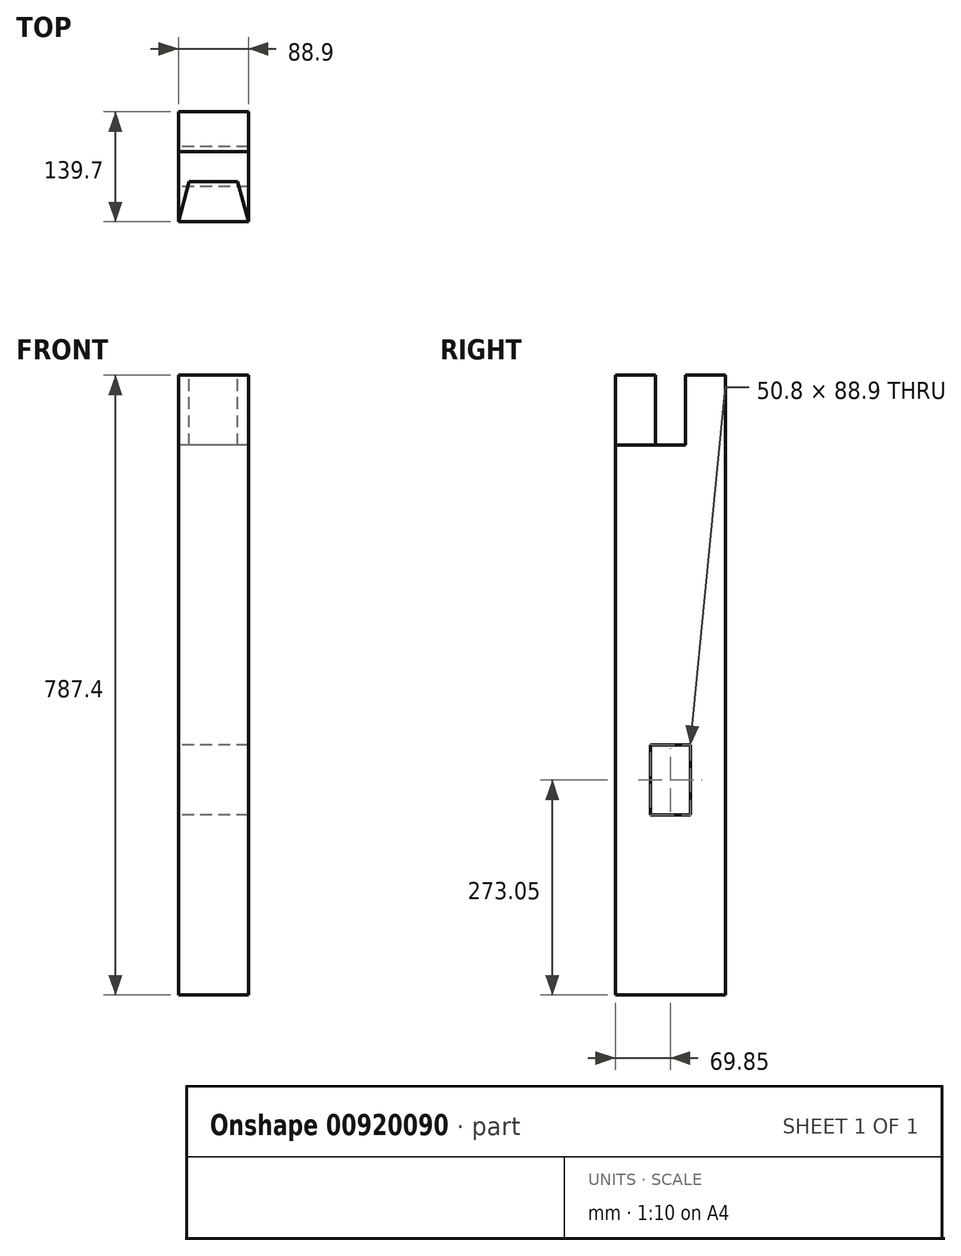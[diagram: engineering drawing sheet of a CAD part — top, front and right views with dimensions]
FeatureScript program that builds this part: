
annotation { "Feature Type Name" : "Feature", "Feature Type Description" : "" }
export const myFeature = defineFeature(function(context is Context, id is Id, definition is map)
    precondition{}
    {
        {
            var Q0;
            Q0=qCreatedBy(makeId("Top.planeOp"),FACE);
            var sketch = newSketch(context, id + "F0", { "sketchPlane" : qUnion([Q0])});
            skLineSegment(sketch, "E0.bottom", {"start": v(0, 0) * mm, "end": v(88.9, 0) * mm});
            skLineSegment(sketch, "E0.top", {"start": v(0, 139.7) * mm, "end": v(88.9, 139.7) * mm});
            skLineSegment(sketch, "E0.left", {"start": v(0, 0) * mm, "end": v(0, 139.7) * mm});
            skLineSegment(sketch, "E0.right", {"start": v(88.9, 0) * mm, "end": v(88.9, 139.7) * mm});
            skSolve(sketch);
        }
        {
            var Q0;
            Q0=makeQuery(id+"F0.imprint","IMPRINT",FACE,{"disambiguationData":[TD([[makeQuery(id+"F0.imprint","IMPRINT",EDGE,{"derivedFrom":sQuery(id+"F0.wireOp",EDGE,"E0.bottom")}),1.0]])]});
            extrude(context, id + "F1", {"entities" : qUnion([Q0]), "depth" : 787.4 * mm, "offsetDistance" : 25.4 * mm});
        }
        {
            var Q0;
            Q0=makeQuery(id+"F1.opExtrude","CAP_FACE",FACE,{"disambiguationData":[OSD([sQuery(id+"F0.wireOp",EDGE,"E0.bottom"),sQuery(id+"F0.wireOp",EDGE,"E0.top"),sQuery(id+"F0.wireOp",EDGE,"E0.left"),sQuery(id+"F0.wireOp",EDGE,"E0.right")])],"isStart":false});
            var sketch = newSketch(context, id + "F2", { "sketchPlane" : qUnion([Q0])});
            skLineSegment(sketch, "E1", {"start": v(0, 0) * mm, "end": v(88.9, 0) * mm});
            skLineSegment(sketch, "E2", {"start": v(88.9, 0) * mm, "end": v(75.29, 50.8) * mm});
            skLineSegment(sketch, "E3", {"start": v(75.29, 50.8) * mm, "end": v(13.61, 50.8) * mm});
            skLineSegment(sketch, "E4", {"start": v(13.61, 50.8) * mm, "end": v(0, 0) * mm});
            skLineSegment(sketch, "E5", {"start": v(0, 139.7) * mm, "end": v(88.9, 139.7) * mm});
            skLineSegment(sketch, "E6", {"start": v(88.9, 139.7) * mm, "end": v(88.9, 88.9) * mm});
            skLineSegment(sketch, "E7", {"start": v(88.9, 88.9) * mm, "end": v(0, 88.9) * mm});
            skLineSegment(sketch, "E8", {"start": v(0, 88.9) * mm, "end": v(0, 139.7) * mm});
            skSolve(sketch);
        }
        {
            var Q0;
            {var subQ2=sQuery(id+"F2.wireOp",EDGE,"E2");Q0=makeQuery(id+"F2.imprint","IMPRINT",FACE,{"disambiguationData":[TD([[makeQuery(id+"F2.imprint","IMPRINT",EDGE,{"derivedFrom":subQ2}),-1.0]])]});}
            extrude(context, id + "F3", {"entities" : qUnion([Q0]), "operationType" : NewBodyOperationType.REMOVE, "oppositeDirection" : true, "depth" : 88.9 * mm, "offsetDistance" : 25.4 * mm});
        }
        {
            var Q0;
            Q0=makeQuery(id+"F1.opExtrude","SWEPT_FACE",FACE,{"disambiguationData":[OSD([sQuery(id+"F0.wireOp",EDGE,"E0.left")])]});
            var sketch = newSketch(context, id + "F4", { "sketchPlane" : qUnion([Q0])});
            skLineSegment(sketch, "E9.bottom", {"start": v(-95.25, 317.5) * mm, "end": v(-44.45, 317.5) * mm});
            skLineSegment(sketch, "E9.top", {"start": v(-95.25, 228.6) * mm, "end": v(-44.45, 228.6) * mm});
            skLineSegment(sketch, "E9.left", {"start": v(-95.25, 317.5) * mm, "end": v(-95.25, 228.6) * mm});
            skLineSegment(sketch, "E9.right", {"start": v(-44.45, 317.5) * mm, "end": v(-44.45, 228.6) * mm});
            skSolve(sketch);
        }
        {
            var Q0;
            Q0=makeQuery(id+"F4.imprint","IMPRINT",FACE,{"disambiguationData":[TD([[makeQuery(id+"F4.imprint","IMPRINT",EDGE,{"derivedFrom":sQuery(id+"F4.wireOp",EDGE,"E9.bottom")}),-1.0]])]});
            extrude(context, id + "F5", {"entities" : qUnion([Q0]), "operationType" : NewBodyOperationType.REMOVE, "endBound" : BoundingType.UP_TO_NEXT, "oppositeDirection" : true, "depth" : 25.4 * mm, "offsetDistance" : 25.4 * mm});
        }
    });
